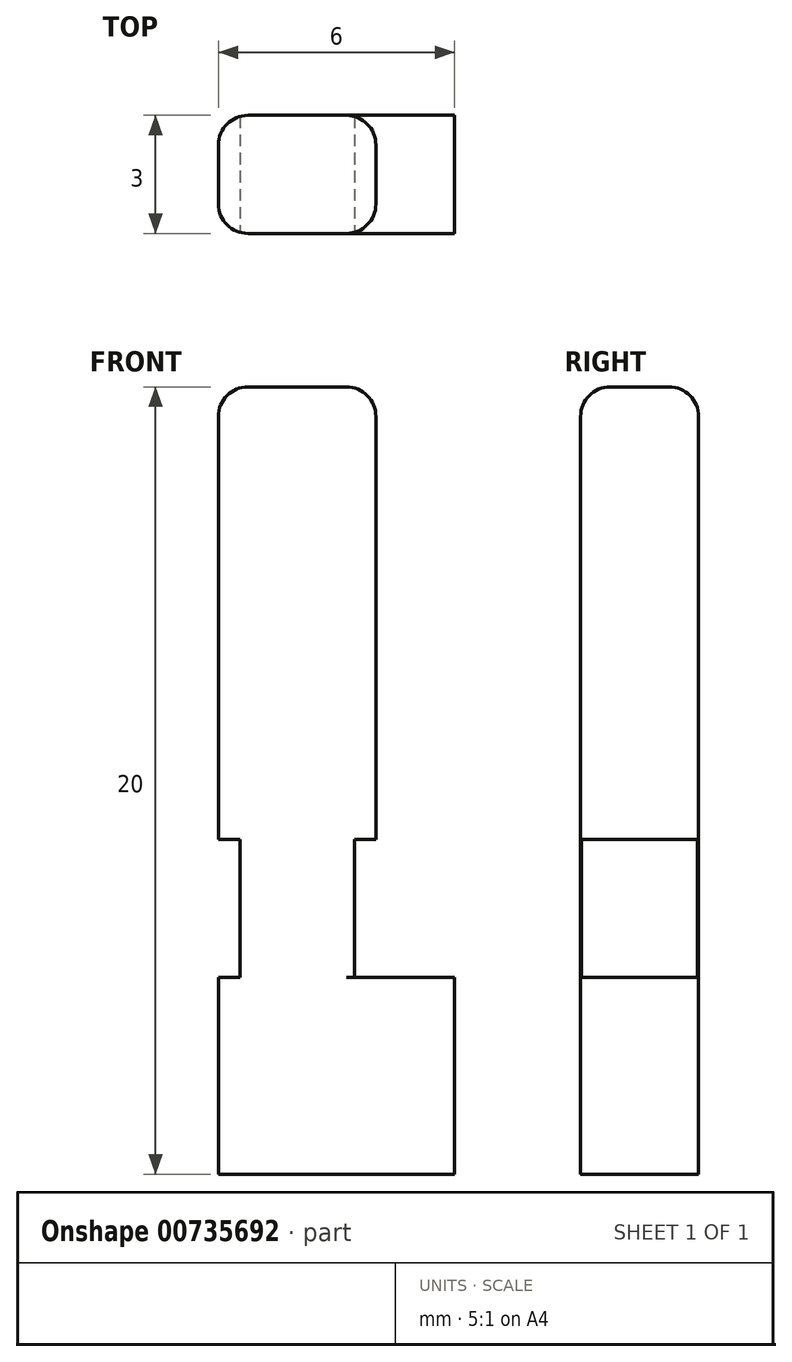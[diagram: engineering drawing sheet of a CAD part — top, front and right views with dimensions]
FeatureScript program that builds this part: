
annotation { "Feature Type Name" : "Feature", "Feature Type Description" : "" }
export const myFeature = defineFeature(function(context is Context, id is Id, definition is map)
    precondition{}
    {
        {
            var Q0;
            Q0=qCreatedBy(makeId("Top.planeOp"),FACE);
            var sketch = newSketch(context, id + "F0", { "sketchPlane" : qUnion([Q0])});
            skLineSegment(sketch, "E0.bottom", {"start": v(-3, 1.5) * mm, "end": v(3, 1.5) * mm});
            skLineSegment(sketch, "E0.top", {"start": v(-3, -1.5) * mm, "end": v(3, -1.5) * mm});
            skLineSegment(sketch, "E0.left", {"start": v(-3, 1.5) * mm, "end": v(-3, -1.5) * mm});
            skLineSegment(sketch, "E0.right", {"start": v(3, 1.5) * mm, "end": v(3, -1.5) * mm});
            skLineSegment(sketch, "E1", {"start": v(-3, 1.5) * mm, "end": v(3, -1.5) * mm, "construction": true});
            skSolve(sketch);
        }
        {
            var Q0;
            Q0=makeQuery(id+"F0.imprint","IMPRINT",FACE,{"disambiguationData":[TD([[makeQuery(id+"F0.imprint","IMPRINT",EDGE,{"derivedFrom":sQuery(id+"F0.wireOp",EDGE,"E0.bottom")}),-1.0]])]});
            extrude(context, id + "F1", {"entities" : qUnion([Q0]), "depth" : 5 * mm, "offsetDistance" : 25 * mm});
        }
        {
            var Q0;
            Q0=makeQuery(id+"F1.opExtrude","CAP_FACE",FACE,{"disambiguationData":[OSD([sQuery(id+"F0.wireOp",EDGE,"E0.bottom"),sQuery(id+"F0.wireOp",EDGE,"E0.top"),sQuery(id+"F0.wireOp",EDGE,"E0.left"),sQuery(id+"F0.wireOp",EDGE,"E0.right")])],"isStart":false});
            var sketch = newSketch(context, id + "F2", { "sketchPlane" : qUnion([Q0])});
            skLineSegment(sketch, "E2.bottom", {"start": v(-3, 1.5) * mm, "end": v(1, 1.5) * mm});
            skLineSegment(sketch, "E2.top", {"start": v(-3, -1.5) * mm, "end": v(1, -1.5) * mm});
            skLineSegment(sketch, "E2.left", {"start": v(-3, 1.5) * mm, "end": v(-3, -1.5) * mm});
            skLineSegment(sketch, "E2.right", {"start": v(1, 1.5) * mm, "end": v(1, -1.5) * mm});
            skSolve(sketch);
        }
        {
            var Q0;
            Q0 = qSketchRegion(id + "F2", true);
            extrude(context, id + "F3", {"entities" : qUnion([Q0]), "operationType" : NewBodyOperationType.ADD, "depth" : 15 * mm, "offsetDistance" : 25 * mm});
        }
        {
            var Q0;
            Q0=makeQuery(id+"F3.boolean.opBoolean","MERGE",FACE,{"derivedFrom":[makeQuery(id+"F1.opExtrude","SWEPT_FACE",FACE,{"disambiguationData":[OSD([sQuery(id+"F0.wireOp",EDGE,"E0.top")])]}),makeQuery(id+"F3.opExtrude","SWEPT_FACE",FACE,{"disambiguationData":[OSD([sQuery(id+"F2.wireOp",EDGE,"E2.top")])]})]});
            var sketch = newSketch(context, id + "F4", { "sketchPlane" : qUnion([Q0])});
            skLineSegment(sketch, "E3.bottom", {"start": v(-2.45, 5) * mm, "end": v(-3.45, 5) * mm});
            skLineSegment(sketch, "E3.top", {"start": v(-2.45, 8.5) * mm, "end": v(-3.45, 8.5) * mm});
            skLineSegment(sketch, "E3.left", {"start": v(-2.45, 5) * mm, "end": v(-2.45, 8.5) * mm});
            skLineSegment(sketch, "E3.right", {"start": v(-3.45, 5) * mm, "end": v(-3.45, 8.5) * mm});
            skLineSegment(sketch, "E4.bottom", {"start": v(1.45, 5) * mm, "end": v(0.45, 5) * mm});
            skLineSegment(sketch, "E4.top", {"start": v(1.45, 8.5) * mm, "end": v(0.45, 8.5) * mm});
            skLineSegment(sketch, "E4.left", {"start": v(1.45, 5) * mm, "end": v(1.45, 8.5) * mm});
            skLineSegment(sketch, "E4.right", {"start": v(0.45, 5) * mm, "end": v(0.45, 8.5) * mm});
            skSolve(sketch);
        }
        {
            var Q0;
            Q0 = qSketchRegion(id + "F4", true);
            extrude(context, id + "F5", {"entities" : qUnion([Q0]), "operationType" : NewBodyOperationType.REMOVE, "oppositeDirection" : true, "depth" : 25 * mm, "offsetDistance" : 25 * mm});
        }
        {
            var Q0;
            Q0=makeQuery(id+"F3.opExtrude","CAP_EDGE",EDGE,{"disambiguationData":[OSD([sQuery(id+"F2.wireOp",EDGE,"E2.bottom")])],"isStart":false});
            var Q1;
            Q1=makeQuery(id+"F3.opExtrude","SWEPT_EDGE",EDGE,{"disambiguationData":[OSD([sQuery(id+"F2.wireOp",EDGE,"E2.bottom"),sQuery(id+"F2.wireOp",EDGE,"E2.left")])]});
            var Q2;
            Q2=makeQuery(id+"F3.opExtrude","SWEPT_EDGE",EDGE,{"disambiguationData":[OSD([sQuery(id+"F2.wireOp",EDGE,"E2.bottom"),sQuery(id+"F2.wireOp",EDGE,"E2.right")])]});
            var Q3;
            Q3=makeQuery(id+"F3.opExtrude","SWEPT_EDGE",EDGE,{"disambiguationData":[OSD([sQuery(id+"F2.wireOp",EDGE,"E2.top"),sQuery(id+"F2.wireOp",EDGE,"E2.left")])]});
            var Q4;
            Q4=makeQuery(id+"F3.opExtrude","CAP_EDGE",EDGE,{"disambiguationData":[OSD([sQuery(id+"F2.wireOp",EDGE,"E2.left")])],"isStart":false});
            var Q5;
            Q5=makeQuery(id+"F3.opExtrude","CAP_EDGE",EDGE,{"disambiguationData":[OSD([sQuery(id+"F2.wireOp",EDGE,"E2.top")])],"isStart":false});
            var Q6;
            Q6=makeQuery(id+"F3.opExtrude","CAP_EDGE",EDGE,{"disambiguationData":[OSD([sQuery(id+"F2.wireOp",EDGE,"E2.right")])],"isStart":false});
            var Q7;
            Q7=makeQuery(id+"F3.opExtrude","SWEPT_EDGE",EDGE,{"disambiguationData":[OSD([sQuery(id+"F2.wireOp",EDGE,"E2.top"),sQuery(id+"F2.wireOp",EDGE,"E2.right")])]});
            fillet(context, id + "F6", {"entities" : qUnion([Q0, Q1, Q2, Q3, Q4, Q5, Q6, Q7]), "radius" : 0.75 * mm, "tangentPropagation" : true, "allowEdgeOverflow" : false});
        }
    });
